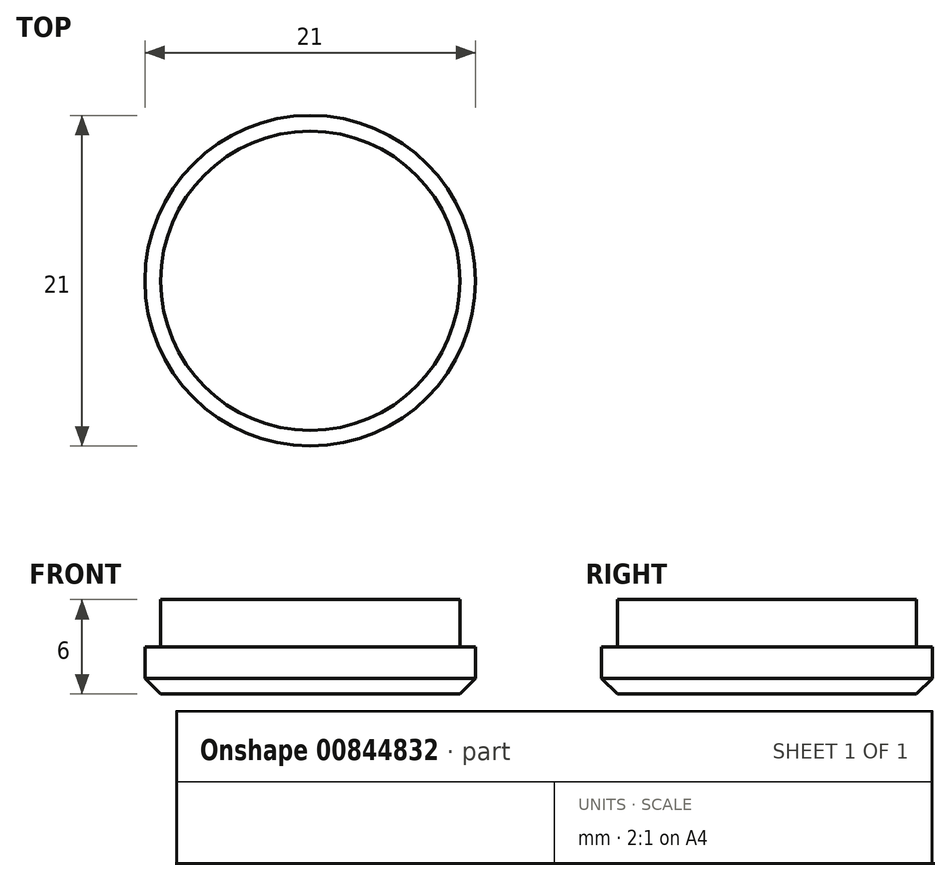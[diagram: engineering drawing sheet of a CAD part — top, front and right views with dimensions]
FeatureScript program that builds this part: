
annotation { "Feature Type Name" : "Feature", "Feature Type Description" : "" }
export const myFeature = defineFeature(function(context is Context, id is Id, definition is map)
    precondition{}
    {
        {
            var Q0;
            Q0=qCreatedBy(makeId("Top.planeOp"),FACE);
            var sketch = newSketch(context, id + "F0", { "sketchPlane" : qUnion([Q0])});
            skCircle(sketch, "E0", {"center": v(0, 0) * mm, "radius": 10.5 * mm});
            skLineSegment(sketch, "E1", {"start": v(0, 0) * mm, "end": v(-5.5, 0) * mm, "construction": true});
            skLineSegment(sketch, "E2", {"start": v(-5.5, 0) * mm, "end": v(-5.5, -8.94) * mm, "construction": true});
            skLineSegment(sketch, "E3", {"start": v(-5.5, -8.94) * mm, "end": v(-5.5, 0) * mm, "construction": true});
            skSolve(sketch);
        }
        {
            var Q0;
            Q0=qSketchRegion(id+"F0",true);
            extrude(context, id + "F1", {"entities" : qUnion([Q0]), "depth" : 3 * mm, "offsetDistance" : 25 * mm});
        }
        {
            var Q0;
            Q0=makeQuery(id+"F1.opExtrude","CAP_EDGE",EDGE,{"disambiguationData":[OSD([sQuery(id+"F0.wireOp",EDGE,"E0")])],"isStart":true});
            chamfer(context, id + "F2", {"entities" : qUnion([Q0]), "width" : 1 * mm, "tangentPropagation" : true});
        }
        {
            var Q0;
            Q0=makeQuery(id+"F1.opExtrude","CAP_FACE",FACE,{"disambiguationData":[OSD([sQuery(id+"F0.wireOp",EDGE,"E0")])],"isStart":false});
            var sketch = newSketch(context, id + "F3", { "sketchPlane" : qUnion([Q0])});
            skCircle(sketch, "E4", {"center": v(0, 0) * mm, "radius": 9.5 * mm});
            skSolve(sketch);
        }
        {
            var Q0;
            Q0=qSketchRegion(id+"F3",true);
            extrude(context, id + "F4", {"entities" : qUnion([Q0]), "operationType" : NewBodyOperationType.ADD, "depth" : 3 * mm, "offsetDistance" : 25 * mm});
        }
    });
